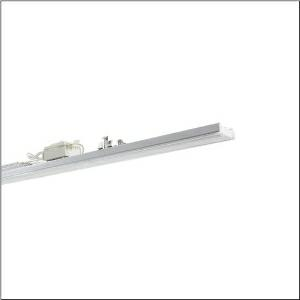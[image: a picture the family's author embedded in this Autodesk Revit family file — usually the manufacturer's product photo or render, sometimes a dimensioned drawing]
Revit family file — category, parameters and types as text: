
# Revit family: licross_r__11_recessed_mo_51te147n48xg_43e7
name_source: partatom
category: Lighting Fixtures
units: mm (PartAtom-declared; Revit-internal decimal feet)

## family parameters
Cut with Voids When Loaded = No
Host = Face
Light Source = No
Part Type = Normal
Room Calculation Point = No
Round Connector Dimension = Use Diameter
Shared = No

## types (1)
- Licross® 11 Recessed MO (1 x LED, 8240 lm, 48.5 W, 4000K)
    Apparent Load = 49 VA
    CIE Flux Codes = 56 84 97 100 100
    Color Rendering = 80
    Color Temperature = 4000K
    Default Elevation = 1800 mm
    Description = Licross® 11 Recessed MO, luminaire insert, of sheet steel, galvanised, coil coated, white, length: 1.500mm, width: 66mm, height: 67mm, LED rated luminous flux: 8.240lm, light colour: 840, control gear: ON/OFF, with plug, 3-pole, with phase selection, mains connection: 220..240V, AC, 50/60Hz, rated input power: 49W, halogen-free wiring, primary light control with lens, of plastic, primary optical cover: cover, of PMMA, light emission: direct distribution, primary light characteristic: asymmetric, protection rating (complete): IP54, insulation class (complete): insulation class I (protective earthing), certification: CE, ENEC, VDE, UKCA, protection symbol: D if used in an environment with non-conductive dust loads with corresponding accessories, impact resistance: IK06, permissible ambient temperature for indoor applications: -35..+35°C, corresponds to IFS (International Featured Standards) requirements for safety and quality in the food industry, reducing of maximum allowable ambient temperature of 5°C with ceiling mounting, packaging unit: 1 piece
    Height = 58 mm
    Lamp = 1 x LED
    Lamp Light Flux = 8240 lm
    Lamp Power = 48.5 W
    Lamp count = 1
    Length = 1500 mm
    Luminous efficacy = 170 lm/W
    Manufacturer = Siteco
    ModVariant = No
    Model = 51TE147N48XG
    Mounting Place = Ceiling
    Mounting Type = Pendant
    Number of Poles = 1
    OnlyDefault = Yes
    Power Factor = 1
    Product Name = Licross® 11 Recessed MO
    Product group = luminaire insert
    ProductGroupID = 902
    Protection Class = Protection class I
    Protection Degree = IP 54
    RLX_Detail_Level = 1
    RLX_Emergency_Light_Flux = 0 lm
    RLX_Emergency_Type = 0
    RLX_Emergency_Type_DB = No
    RlxData = <blob elided: 21273 chars, md5=27ebc0d5>
    Socket = socket
    Standby Power = 0 W
    System Light Flux = 8240 lm
    System Power = 49 W
    Type Comments = Product without accessories
    Type Image = l_1296930.jpg
    URL = http://relux.com
    VarID = ---
    Voltage = 0 V
    Weight = 0.00 kg
    Width = 66 mm

## geometry (parser evidence)
native form markers: Blend x4, Sweep x11
no freeform markers — native parametric forms only
